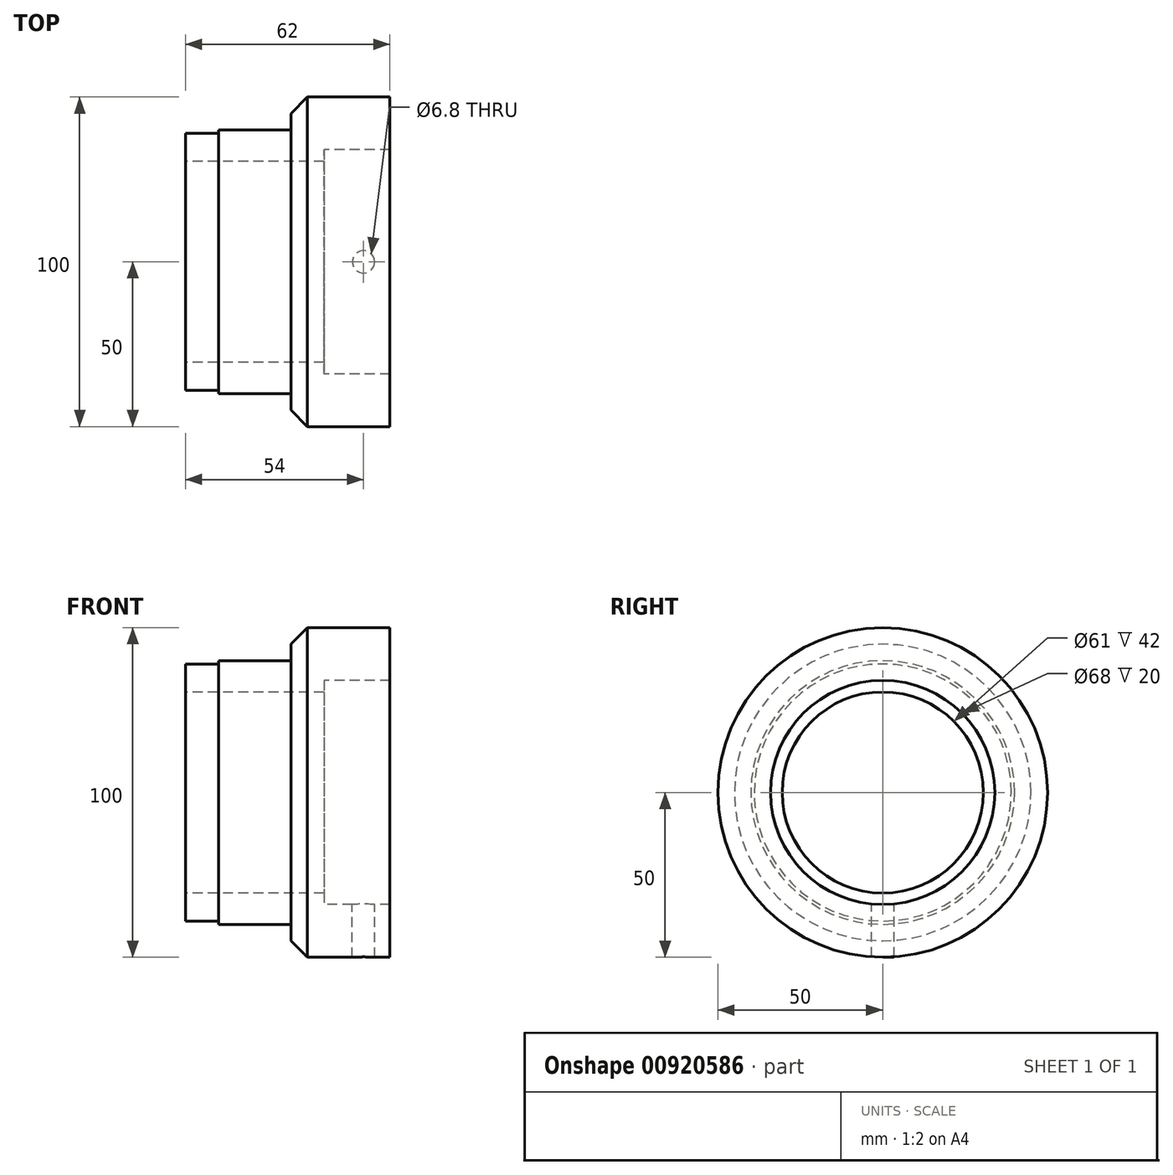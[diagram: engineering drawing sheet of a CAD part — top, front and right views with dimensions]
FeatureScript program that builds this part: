
annotation { "Feature Type Name" : "Feature", "Feature Type Description" : "" }
export const myFeature = defineFeature(function(context is Context, id is Id, definition is map)
    precondition{}
    {
        {
            var Q0;
            Q0=qCreatedBy(makeId("Front.planeOp"),FACE);
            var sketch = newSketch(context, id + "F0", { "sketchPlane" : qUnion([Q0])});
            skLineSegment(sketch, "E0", {"start": v(0, 0) * mm, "end": v(40.39, 0) * mm, "construction": true});
            skLineSegment(sketch, "E1", {"start": v(0, 30.5) * mm, "end": v(42, 30.5) * mm});
            skLineSegment(sketch, "E2", {"start": v(62, 34) * mm, "end": v(62, 50) * mm});
            skLineSegment(sketch, "E3", {"start": v(62, 50) * mm, "end": v(32, 50) * mm});
            skLineSegment(sketch, "E4", {"start": v(32, 50) * mm, "end": v(32, 40) * mm});
            skLineSegment(sketch, "E5", {"start": v(32, 40) * mm, "end": v(10, 40) * mm});
            skLineSegment(sketch, "E6", {"start": v(10, 40) * mm, "end": v(10, 39) * mm});
            skLineSegment(sketch, "E7", {"start": v(10, 39) * mm, "end": v(0, 39) * mm});
            skLineSegment(sketch, "E8", {"start": v(0, 39) * mm, "end": v(0, 30.5) * mm});
            skLineSegment(sketch, "E9", {"start": v(42, 30.5) * mm, "end": v(42, 34) * mm});
            skLineSegment(sketch, "E10", {"start": v(42, 34) * mm, "end": v(62, 34) * mm});
            skSolve(sketch);
        }
        {
            var Q0;
            Q0=makeQuery(id+"F0.imprint","IMPRINT",FACE,{"disambiguationData":[TD([[makeQuery(id+"F0.imprint","IMPRINT",EDGE,{"derivedFrom":sQuery(id+"F0.wireOp",EDGE,"E1")}),1.0]])]});
            var Q1;
            Q1=sQuery(id+"F0.wireOp",EDGE,"E0");
            revolve(context, id + "F1", {"surfaceOperationType" : NewSurfaceOperationType.NEW, "entities" : qUnion([Q0]), "axis" : qUnion([Q1]), "revolveType" : RevolveType.FULL});
        }
        {
            var Q0;
            Q0=makeQuery(id+"F1.opRevolve","SWEPT_EDGE",EDGE,{"disambiguationData":[OSD([sQuery(id+"F0.wireOp",EDGE,"E3"),sQuery(id+"F0.wireOp",EDGE,"E4")])]});
            chamfer(context, id + "F2", {"entities" : qUnion([Q0]), "width" : 5 * mm, "tangentPropagation" : true});
        }
        {
            var Q0;
            Q0=qCreatedBy(makeId("Top.planeOp"),FACE);
            var sketch = newSketch(context, id + "F3", { "sketchPlane" : qUnion([Q0])});
            skCircle(sketch, "E11", {"center": v(54, 0) * mm, "radius": 3.4 * mm});
            skSolve(sketch);
        }
        {
            var Q0;
            Q0=makeQuery(id+"F3.imprint","IMPRINT",FACE,{"disambiguationData":[TD([[makeQuery(id+"F3.imprint","IMPRINT",EDGE,{"derivedFrom":sQuery(id+"F3.wireOp",EDGE,"E11")}),1.0]])]});
            extrude(context, id + "F4", {"entities" : qUnion([Q0]), "operationType" : NewBodyOperationType.REMOVE, "endBound" : BoundingType.THROUGH_ALL, "oppositeDirection" : true, "depth" : 25 * mm, "offsetDistance" : 25 * mm});
        }
    });
